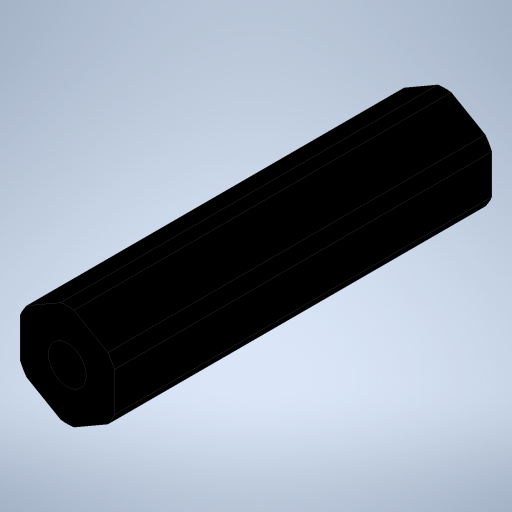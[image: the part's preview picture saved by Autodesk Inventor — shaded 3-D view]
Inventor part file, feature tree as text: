
AUTODESK INVENTOR PART (.ipt)
format: ipt  version: 2023.3 (Build 273359000, 359)  size: 249,344 bytes
history: native  units: in
note: dims shown in document units (in); Inventor stores cm internally (conversion verified against a paired STEP export)
features: sketch x3, extrude x2, projected_geometry x2, hole x1
ambient origin geometry x8: Origin, YZ Plane, XZ Plane, XY Plane, X Axis, Y Axis, Z Axis, Center Point
bodies: Solid1 (feature_tree)
feature tree (8):
  extrude  "Extrusion1"  Depth=1.0in
  hole  "Hole1"  [1 undecoded]
  extrude  "Extrusion3"  [1 undecoded]
  sketch  "Sketch1"  dims[d2=0.0in]
  sketch  "Sketch3"  dims[d9=0.625in d10=0.385in d11=0.25in d12=0.5635in d13=1.0in d14=0.8108in d16=0.7in]
  sketch  "Sketch4"  dims[d17=0.0in d18=0.0in]
  projected_geometry  "Project Cut Edges1"
  projected_geometry  "Project Cut Edges2"
note: 2 required parameter values undecoded (feature->parameter linkage not recoverable at this tier; creation-order binding heuristic only, values carry confidence <= 0.55)
